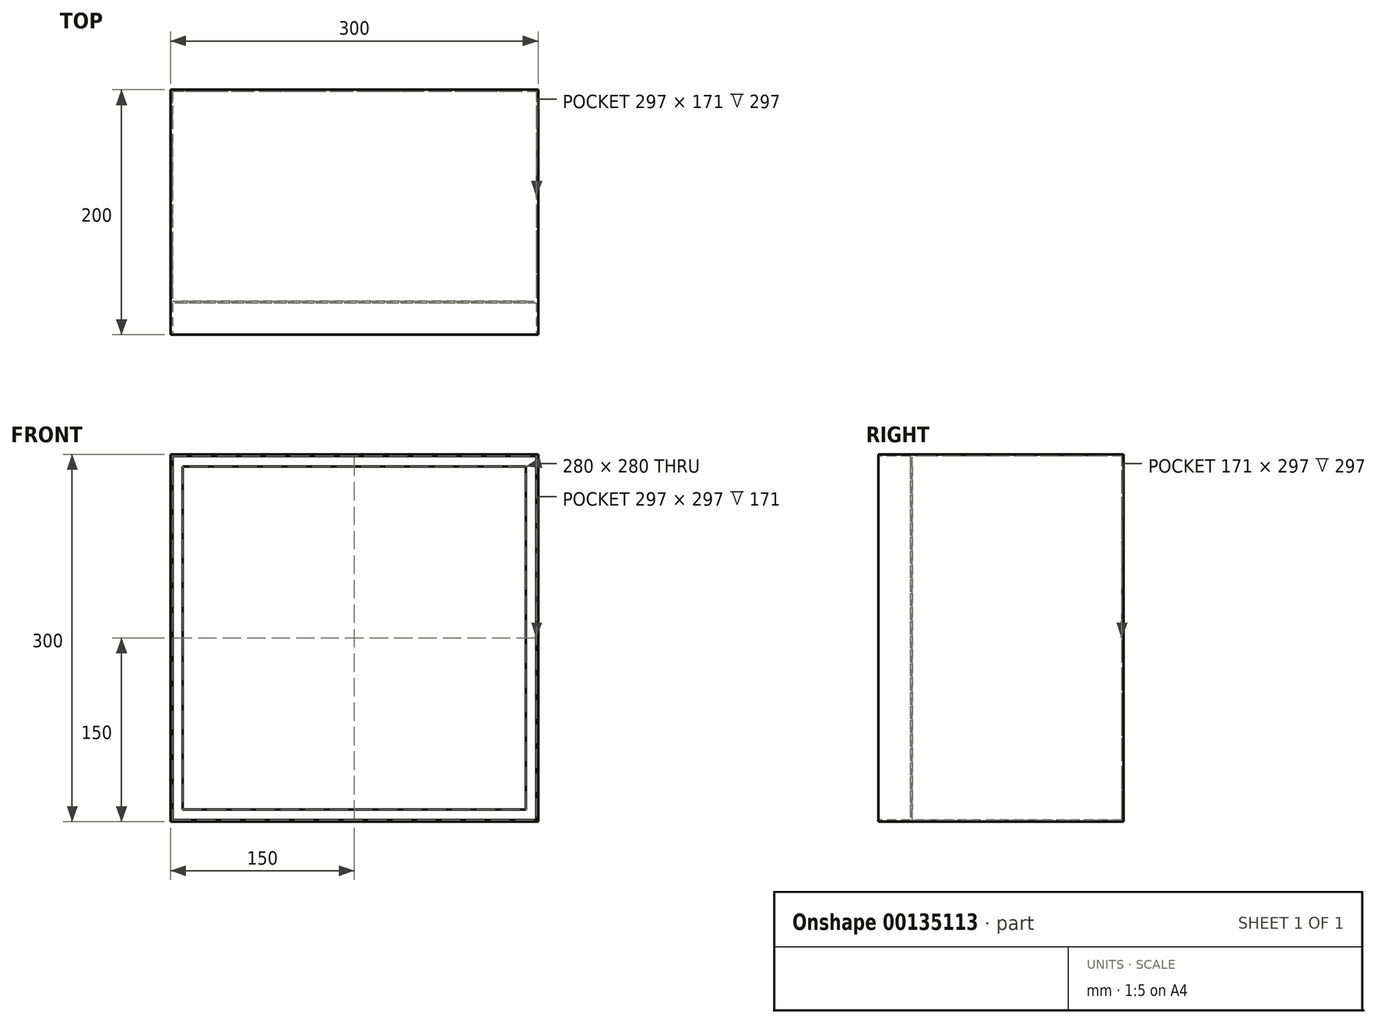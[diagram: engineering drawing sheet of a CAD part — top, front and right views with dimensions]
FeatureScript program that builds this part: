
annotation { "Feature Type Name" : "Feature", "Feature Type Description" : "" }
export const myFeature = defineFeature(function(context is Context, id is Id, definition is map)
    precondition{}
    {
        {
            var Q0;
            Q0=qCreatedBy(makeId("Front.planeOp"),FACE);
            var sketch = newSketch(context, id + "F0", { "sketchPlane" : qUnion([Q0])});
            skLineSegment(sketch, "E0.bottom", {"start": v(150, 150) * mm, "end": v(-150, 150) * mm});
            skLineSegment(sketch, "E0.top", {"start": v(150, -150) * mm, "end": v(-150, -150) * mm});
            skLineSegment(sketch, "E0.left", {"start": v(150, 150) * mm, "end": v(150, -150) * mm});
            skLineSegment(sketch, "E0.right", {"start": v(-150, 150) * mm, "end": v(-150, -150) * mm});
            skPoint(sketch, "E0.middle", {"position": v(0, 0) * mm});
            skSolve(sketch);
        }
        {
            var Q0;
            Q0=makeQuery(id+"F0.imprint","IMPRINT",FACE,{"disambiguationData":[TD([[makeQuery(id+"F0.imprint","IMPRINT",EDGE,{"derivedFrom":sQuery(id+"F0.wireOp",EDGE,"E0.bottom")}),1.0]])]});
            extrude(context, id + "F1", {"entities" : qUnion([Q0]), "depth" : 200 * mm});
        }
        {
            var Q0;
            Q0=makeQuery(id+"F1.opExtrude","CAP_FACE",FACE,{"disambiguationData":[OSD([sQuery(id+"F0.wireOp",EDGE,"E0.bottom"),sQuery(id+"F0.wireOp",EDGE,"E0.top"),sQuery(id+"F0.wireOp",EDGE,"E0.left"),sQuery(id+"F0.wireOp",EDGE,"E0.right")])],"isStart":false});
            var sketch = newSketch(context, id + "F2", { "sketchPlane" : qUnion([Q0])});
            skLineSegment(sketch, "E1.bottom", {"start": v(148.5, 148.5) * mm, "end": v(-148.5, 148.5) * mm});
            skLineSegment(sketch, "E1.top", {"start": v(148.5, -148.5) * mm, "end": v(-148.5, -148.5) * mm});
            skLineSegment(sketch, "E1.left", {"start": v(148.5, 148.5) * mm, "end": v(148.5, -148.5) * mm});
            skLineSegment(sketch, "E1.right", {"start": v(-148.5, 148.5) * mm, "end": v(-148.5, -148.5) * mm});
            skPoint(sketch, "E1.middle", {"position": v(0, 0) * mm});
            skSolve(sketch);
        }
        {
            var Q0;
            Q0=makeQuery(id+"F2.imprint","IMPRINT",FACE,{"disambiguationData":[TD([[makeQuery(id+"F2.imprint","IMPRINT",EDGE,{"derivedFrom":sQuery(id+"F2.wireOp",EDGE,"E1.bottom")}),1.0]])]});
            extrude(context, id + "F3", {"entities" : qUnion([Q0]), "operationType" : NewBodyOperationType.REMOVE, "oppositeDirection" : true, "depth" : 198.5 * mm});
        }
        {
            var Q0;
            Q0=makeQuery(id+"F1.opExtrude","SWEPT_FACE",FACE,{"disambiguationData":[OSD([sQuery(id+"F0.wireOp",EDGE,"E0.left")])]});
            var sketch = newSketch(context, id + "F4", { "sketchPlane" : qUnion([Q0])});
            skLineSegment(sketch, "E2", {"start": v(-200, 0) * mm, "end": v(-174, 0) * mm});
            skLineSegment(sketch, "E3", {"start": v(-174, 0) * mm, "end": v(-174, 150) * mm});
            skLineSegment(sketch, "E4", {"start": v(-174, 150) * mm, "end": v(-172.5, 150) * mm});
            skLineSegment(sketch, "E5", {"start": v(-172.5, 150) * mm, "end": v(-172.5, -150) * mm});
            skLineSegment(sketch, "E6", {"start": v(-172.5, -150) * mm, "end": v(-174, -150) * mm});
            skLineSegment(sketch, "E7", {"start": v(-174, -150) * mm, "end": v(-174, 0) * mm});
            skSolve(sketch);
        }
        {
            var Q0;
            Q0=makeQuery(id+"F4.imprint","IMPRINT",FACE,{"disambiguationData":[TD([[makeQuery(id+"F4.imprint","IMPRINT",EDGE,{"derivedFrom":sQuery(id+"F4.wireOp",EDGE,"E3")}),-1.0]])]});
            extrude(context, id + "F5", {"entities" : qUnion([Q0]), "operationType" : NewBodyOperationType.ADD, "oppositeDirection" : true, "depth" : 300 * mm});
        }
        {
            var Q0;
            Q0=makeQuery(id+"F5.opExtrude","SWEPT_FACE",FACE,{"disambiguationData":[OSD([sQuery(id+"F4.wireOp",EDGE,"E3"),sQuery(id+"F4.wireOp",EDGE,"E7")])]});
            var sketch = newSketch(context, id + "F6", { "sketchPlane" : qUnion([Q0])});
            skLineSegment(sketch, "E8.bottom", {"start": v(140, 140) * mm, "end": v(-140, 140) * mm});
            skLineSegment(sketch, "E8.top", {"start": v(140, -140) * mm, "end": v(-140, -140) * mm});
            skLineSegment(sketch, "E8.left", {"start": v(140, 140) * mm, "end": v(140, -140) * mm});
            skLineSegment(sketch, "E8.right", {"start": v(-140, 140) * mm, "end": v(-140, -140) * mm});
            skPoint(sketch, "E8.middle", {"position": v(0, 0) * mm});
            skSolve(sketch);
        }
        {
            var Q0;
            Q0=makeQuery(id+"F6.imprint","IMPRINT",FACE,{"disambiguationData":[TD([[makeQuery(id+"F6.imprint","IMPRINT",EDGE,{"derivedFrom":sQuery(id+"F6.wireOp",EDGE,"E8.bottom")}),1.0]])]});
            extrude(context, id + "F7", {"entities" : qUnion([Q0]), "operationType" : NewBodyOperationType.REMOVE, "oppositeDirection" : true, "depth" : 25 * mm});
        }
    });
